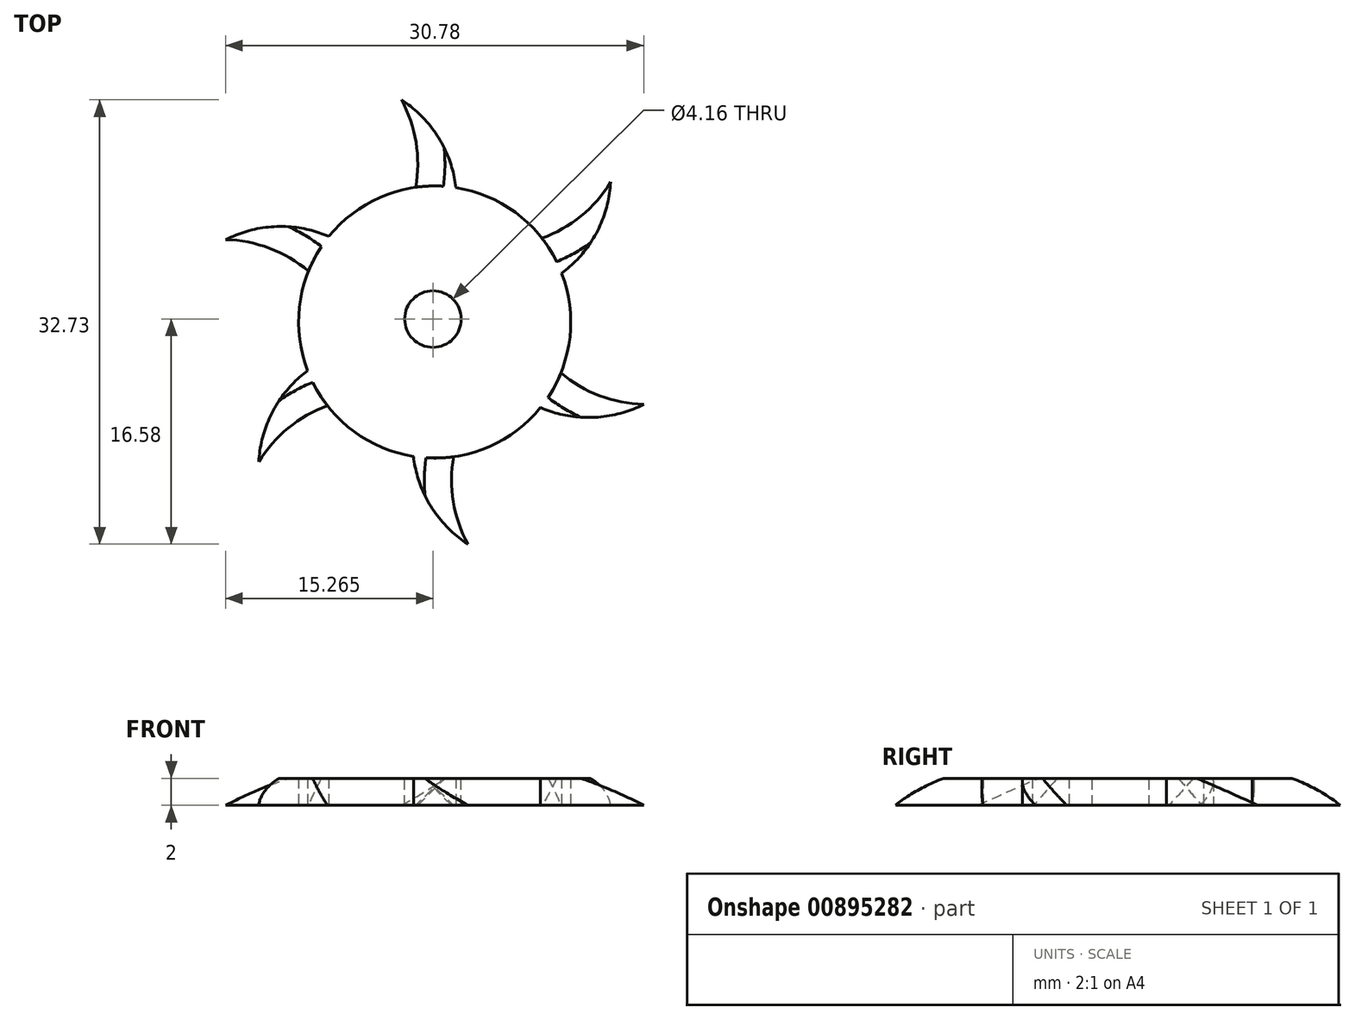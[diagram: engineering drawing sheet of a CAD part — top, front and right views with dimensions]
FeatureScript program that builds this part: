
annotation { "Feature Type Name" : "Feature", "Feature Type Description" : "" }
export const myFeature = defineFeature(function(context is Context, id is Id, definition is map)
    precondition{}
    {
        {
            var Q0;
            Q0=qCreatedBy(makeId("Top.planeOp"),FACE);
            var sketch = newSketch(context, id + "F0", { "sketchPlane" : qUnion([Q0])});
            skCircle(sketch, "E0", {"center": v(-36.95, 32.13) * mm, "radius": 10.02 * mm});
            skArc(sketch, "E1", {"start": v(-41.84, 40.88) * mm, "mid": v(-41.58, 46.04) * mm, "end": v(-45, 49.92) * mm});
            skArc(sketch, "E2", {"start": v(-35.39, 42.03) * mm, "mid": v(-38.6, 47.91) * mm, "end": v(-45, 49.92) * mm});
            skArc(sketch, "E3.1.0", {"start": v(-46.97, 32.27) * mm, "mid": v(-51.3, 35.08) * mm, "end": v(-56.37, 34.06) * mm});
            skArc(sketch, "E3.1.1", {"start": v(-44.74, 38.44) * mm, "mid": v(-51.44, 38.6) * mm, "end": v(-56.37, 34.06) * mm});
            skArc(sketch, "E3.2.0", {"start": v(-42.08, 23.52) * mm, "mid": v(-46.68, 21.17) * mm, "end": v(-48.33, 16.28) * mm});
            skArc(sketch, "E3.2.1", {"start": v(-46.3, 28.54) * mm, "mid": v(-49.8, 22.82) * mm, "end": v(-48.33, 16.28) * mm});
            skArc(sketch, "E3.3.0", {"start": v(-32.06, 23.38) * mm, "mid": v(-32.33, 18.22) * mm, "end": v(-28.91, 14.35) * mm});
            skArc(sketch, "E3.3.1", {"start": v(-38.52, 22.23) * mm, "mid": v(-35.3, 16.35) * mm, "end": v(-28.91, 14.35) * mm});
            skArc(sketch, "E3.4.0", {"start": v(-26.93, 32) * mm, "mid": v(-22.6, 29.18) * mm, "end": v(-17.53, 30.2) * mm});
            skArc(sketch, "E3.4.1", {"start": v(-29.16, 25.83) * mm, "mid": v(-22.46, 25.67) * mm, "end": v(-17.53, 30.2) * mm});
            skArc(sketch, "E3.5.0", {"start": v(-31.82, 40.74) * mm, "mid": v(-27.22, 43.1) * mm, "end": v(-25.57, 47.99) * mm});
            skArc(sketch, "E3.5.1", {"start": v(-27.6, 35.73) * mm, "mid": v(-24.1, 41.45) * mm, "end": v(-25.57, 47.99) * mm});
            skSolve(sketch);
        }
        {
            var Q0;
            {var subQ0=sQuery(id+"F0.wireOp",EDGE,"E0");var subQ8=makeQuery(id+"F0.imprint","INTERSECT",VERTEX,{"derivedFrom":[subQ0,sQuery(id+"F0.wireOp",EDGE,"E3.5.0")]});Q0=makeQuery(id+"F0.imprint","IMPRINT",FACE,{"disambiguationData":[TD([[makeQuery(id+"F0.imprint","IMPRINT",EDGE,{"disambiguationData":[TD([[subQ8,1.0]])],"derivedFrom":subQ0}),1.0]])]});}
            var Q1;
            {var subQ0=sQuery(id+"F0.wireOp",EDGE,"E3.1.0");Q1=makeQuery(id+"F0.imprint","IMPRINT",FACE,{"disambiguationData":[TD([[makeQuery(id+"F0.imprint","IMPRINT",EDGE,{"derivedFrom":subQ0}),-1.0]])]});}
            var Q2;
            {var subQ0=sQuery(id+"F0.wireOp",EDGE,"E3.2.0");Q2=makeQuery(id+"F0.imprint","IMPRINT",FACE,{"disambiguationData":[TD([[makeQuery(id+"F0.imprint","IMPRINT",EDGE,{"derivedFrom":subQ0}),-1.0]])]});}
            var Q3;
            {var subQ0=sQuery(id+"F0.wireOp",EDGE,"E1");Q3=makeQuery(id+"F0.imprint","IMPRINT",FACE,{"disambiguationData":[TD([[makeQuery(id+"F0.imprint","IMPRINT",EDGE,{"derivedFrom":subQ0}),-1.0]])]});}
            var Q4;
            {var subQ0=sQuery(id+"F0.wireOp",EDGE,"E3.5.0");Q4=makeQuery(id+"F0.imprint","IMPRINT",FACE,{"disambiguationData":[TD([[makeQuery(id+"F0.imprint","IMPRINT",EDGE,{"derivedFrom":subQ0}),-1.0]])]});}
            var Q5;
            {var subQ0=sQuery(id+"F0.wireOp",EDGE,"E3.4.0");Q5=makeQuery(id+"F0.imprint","IMPRINT",FACE,{"disambiguationData":[TD([[makeQuery(id+"F0.imprint","IMPRINT",EDGE,{"derivedFrom":subQ0}),-1.0]])]});}
            var Q6;
            {var subQ0=sQuery(id+"F0.wireOp",EDGE,"E3.3.0");Q6=makeQuery(id+"F0.imprint","IMPRINT",FACE,{"disambiguationData":[TD([[makeQuery(id+"F0.imprint","IMPRINT",EDGE,{"derivedFrom":subQ0}),-1.0]])]});}
            extrude(context, id + "F1", {"entities" : qUnion([Q0, Q1, Q2, Q3, Q4, Q5, Q6]), "depth" : 2 * mm, "offsetDistance" : 25 * mm});
        }
        {
            var Q0;
            Q0=makeQuery(id+"F1.opExtrude","CAP_EDGE",EDGE,{"disambiguationData":[OSD([sQuery(id+"F0.wireOp",EDGE,"E3.1.0")])],"isStart":false});
            var Q1;
            Q1=makeQuery(id+"F1.opExtrude","CAP_EDGE",EDGE,{"disambiguationData":[OSD([sQuery(id+"F0.wireOp",EDGE,"E3.2.0")])],"isStart":false});
            var Q2;
            Q2=makeQuery(id+"F1.opExtrude","CAP_EDGE",EDGE,{"disambiguationData":[OSD([sQuery(id+"F0.wireOp",EDGE,"E3.3.0")])],"isStart":false});
            var Q3;
            Q3=makeQuery(id+"F1.opExtrude","CAP_EDGE",EDGE,{"disambiguationData":[OSD([sQuery(id+"F0.wireOp",EDGE,"E3.4.0")])],"isStart":false});
            var Q4;
            Q4=makeQuery(id+"F1.opExtrude","CAP_EDGE",EDGE,{"disambiguationData":[OSD([sQuery(id+"F0.wireOp",EDGE,"E3.5.0")])],"isStart":false});
            var Q5;
            Q5=makeQuery(id+"F1.opExtrude","CAP_EDGE",EDGE,{"disambiguationData":[OSD([sQuery(id+"F0.wireOp",EDGE,"E1")])],"isStart":false});
            chamfer(context, id + "F2", {"entities" : qUnion([Q0, Q1, Q2, Q3, Q4, Q5]), "width" : 5 * mm, "tangentPropagation" : true});
        }
        {
            var Q0;
            Q0=makeQuery(id+"F1.opExtrude","CAP_FACE",FACE,{"disambiguationData":[OSD([sQuery(id+"F0.wireOp",EDGE,"E0"),sQuery(id+"F0.wireOp",EDGE,"E1"),sQuery(id+"F0.wireOp",EDGE,"E2"),sQuery(id+"F0.wireOp",EDGE,"E3.1.0"),sQuery(id+"F0.wireOp",EDGE,"E3.1.1"),sQuery(id+"F0.wireOp",EDGE,"E3.2.0"),sQuery(id+"F0.wireOp",EDGE,"E3.2.1"),sQuery(id+"F0.wireOp",EDGE,"E3.3.0"),sQuery(id+"F0.wireOp",EDGE,"E3.3.1"),sQuery(id+"F0.wireOp",EDGE,"E3.4.0"),sQuery(id+"F0.wireOp",EDGE,"E3.4.1"),sQuery(id+"F0.wireOp",EDGE,"E3.5.0"),sQuery(id+"F0.wireOp",EDGE,"E3.5.1")])],"isStart":false});
            var sketch = newSketch(context, id + "F3", { "sketchPlane" : qUnion([Q0])});
            skSolve(sketch);
        }
        {
            var Q0;
            {var subQ7=sQuery(id+"F0.wireOp",EDGE,"E2");Q0=makeQuery(id+"F3.imprint","IMPRINT",FACE,{"disambiguationData":[TD([[makeQuery(id+"F3.imprint","IMPRINT",EDGE,{"derivedFrom":makeQuery(id+"F1.opExtrude","CAP_EDGE",EDGE,{"disambiguationData":[OSD([subQ7])],"isStart":false})}),1.0]])]});}
            var sketch = newSketch(context, id + "F4", { "sketchPlane" : qUnion([Q0])});
            skCircle(sketch, "E4", {"center": v(-37.07, 32.35) * mm, "radius": 2.08 * mm});
            skSolve(sketch);
        }
        {
            var Q0;
            Q0=makeQuery(id+"F4.imprint","IMPRINT",FACE,{"disambiguationData":[TD([[makeQuery(id+"F4.imprint","IMPRINT",EDGE,{"derivedFrom":sQuery(id+"F4.wireOp",EDGE,"E4")}),1.0]])]});
            extrude(context, id + "F5", {"entities" : qUnion([Q0]), "operationType" : NewBodyOperationType.REMOVE, "oppositeDirection" : true, "depth" : 25 * mm, "offsetDistance" : 25 * mm});
        }
    });
